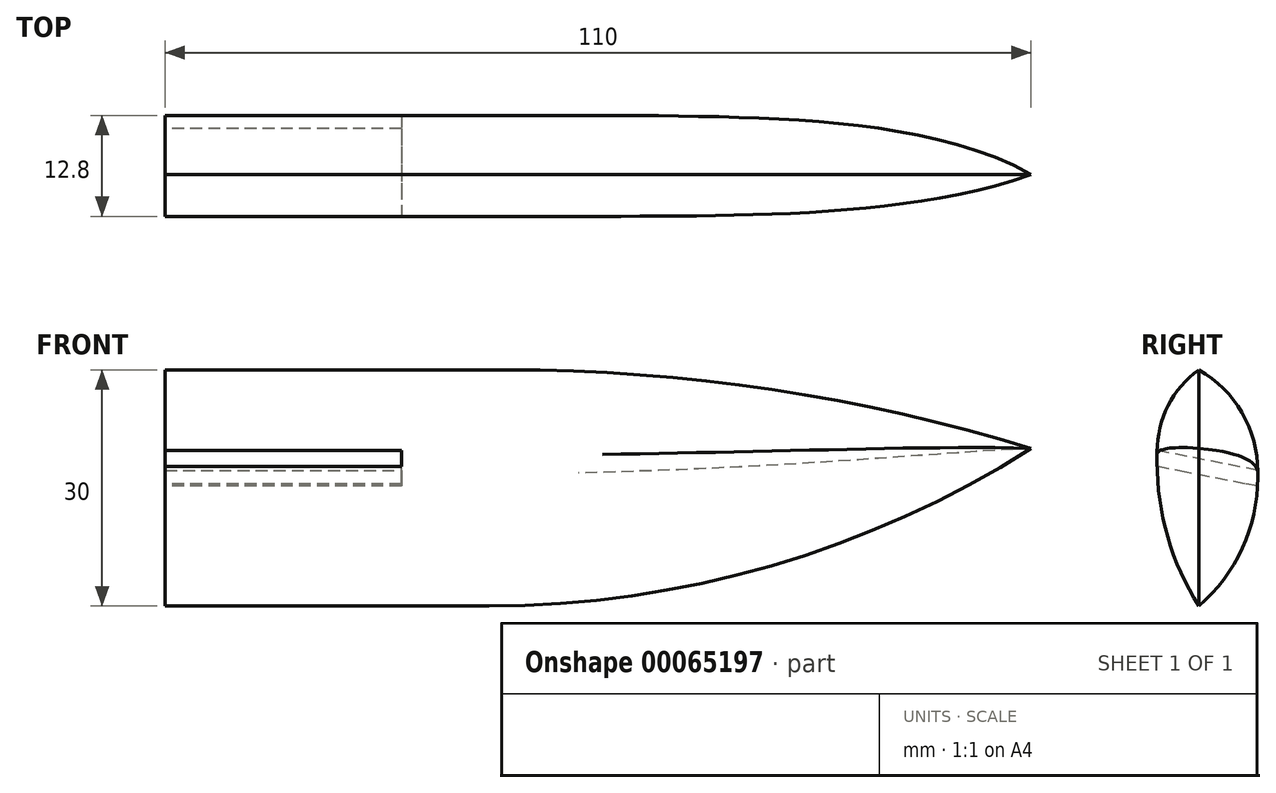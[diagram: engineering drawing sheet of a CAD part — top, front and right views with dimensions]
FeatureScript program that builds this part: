
annotation { "Feature Type Name" : "Feature", "Feature Type Description" : "" }
export const myFeature = defineFeature(function(context is Context, id is Id, definition is map)
    precondition{}
    {
        {
            var Q0;
            Q0=qCreatedBy(makeId("Front.planeOp"),FACE);
            var sketch = newSketch(context, id + "F0", { "sketchPlane" : qUnion([Q0])});
            skLineSegment(sketch, "E0", {"start": v(0, 0) * mm, "end": v(110, 0) * mm});
            skLineSegment(sketch, "E1", {"start": v(110, 0) * mm, "end": v(110, -30) * mm});
            skLineSegment(sketch, "E2", {"start": v(110, -30) * mm, "end": v(0, -30) * mm});
            skLineSegment(sketch, "E3", {"start": v(0, -30) * mm, "end": v(0, 0) * mm});
            skSolve(sketch);
        }
        {
            var Q0;
            Q0 = qSketchRegion(id + "F0", true);
            extrude(context, id + "F1", {"entities" : qUnion([Q0]), "depth" : 5.3 * mm});
        }
        {
            var Q0;
            Q0=makeQuery(id+"F1.opExtrude","SWEPT_EDGE",EDGE,{"disambiguationData":[OSD([sQuery(id+"F0.wireOp",EDGE,"E0"),sQuery(id+"F0.wireOp",EDGE,"E1")])]});
            chamfer(context, id + "F2", {"entities" : qUnion([Q0]), "width" : 20 * mm, "tangentPropagation" : true});
        }
        {
            var Q0;
            Q0=makeQuery(id+"F1.opExtrude","SWEPT_EDGE",EDGE,{"disambiguationData":[OSD([sQuery(id+"F0.wireOp",EDGE,"E1"),sQuery(id+"F0.wireOp",EDGE,"E2")])]});
            chamfer(context, id + "F3", {"entities" : qUnion([Q0]), "width" : 30 * mm, "tangentPropagation" : true});
        }
        {
            var Q0;
            {var subQ0=sQuery(id+"F0.wireOp",EDGE,"E0");Q0=makeQuery(id+"F2.opChamfer","BLEND_EDGE",EDGE,{"blendedFrom":[makeQuery(id+"F1.opExtrude","SWEPT_EDGE",EDGE,{"disambiguationData":[OSD([subQ0,sQuery(id+"F0.wireOp",EDGE,"E1")])]}),makeQuery(id+"F1.opExtrude","SWEPT_FACE",FACE,{"disambiguationData":[OSD([subQ0])]})],"blendedInto":[makeQuery(id+"F1.opExtrude","SWEPT_FACE",FACE,{"disambiguationData":[OSD([subQ0])]})]});}
            fillet(context, id + "F4", {"entities" : qUnion([Q0]), "radius" : 226.64 * mm, "tangentPropagation" : true, "allowEdgeOverflow" : false});
        }
        {
            var Q0;
            {var subQ0=sQuery(id+"F0.wireOp",EDGE,"E2");Q0=makeQuery(id+"F3.opChamfer","BLEND_EDGE",EDGE,{"blendedFrom":[makeQuery(id+"F1.opExtrude","SWEPT_EDGE",EDGE,{"disambiguationData":[OSD([sQuery(id+"F0.wireOp",EDGE,"E1"),subQ0])]}),makeQuery(id+"F1.opExtrude","SWEPT_FACE",FACE,{"disambiguationData":[OSD([subQ0])]})],"blendedInto":[makeQuery(id+"F1.opExtrude","SWEPT_FACE",FACE,{"disambiguationData":[OSD([subQ0])]})]});}
            fillet(context, id + "F5", {"entities" : qUnion([Q0]), "radius" : 128.58 * mm, "tangentPropagation" : true, "allowEdgeOverflow" : false});
        }
        {
            var Q0;
            Q0=makeQuery(id+"F1.opExtrude","CAP_EDGE",EDGE,{"disambiguationData":[OSD([sQuery(id+"F0.wireOp",EDGE,"E0")])],"isStart":false});
            var Q1;
            {var subQ0=sQuery(id+"F0.wireOp",EDGE,"E1");var subQ1=sQuery(id+"F0.wireOp",EDGE,"E0");Q1=makeQuery(id+"F4.opFillet","BLEND_EDGE",EDGE,{"blendedFrom":[makeQuery(id+"F2.opChamfer","BLEND_EDGE",EDGE,{"blendedFrom":[makeQuery(id+"F1.opExtrude","SWEPT_EDGE",EDGE,{"disambiguationData":[OSD([subQ1,subQ0])]}),makeQuery(id+"F1.opExtrude","SWEPT_FACE",FACE,{"disambiguationData":[OSD([subQ1])]})],"blendedInto":[makeQuery(id+"F1.opExtrude","SWEPT_FACE",FACE,{"disambiguationData":[OSD([subQ1])]})]}),makeQuery(id+"F1.opExtrude","CAP_FACE",FACE,{"disambiguationData":[OSD([subQ1,subQ0,sQuery(id+"F0.wireOp",EDGE,"E2"),sQuery(id+"F0.wireOp",EDGE,"E3")])],"isStart":false})],"blendedInto":[makeQuery(id+"F1.opExtrude","CAP_FACE",FACE,{"disambiguationData":[OSD([subQ1,subQ0,sQuery(id+"F0.wireOp",EDGE,"E2"),sQuery(id+"F0.wireOp",EDGE,"E3")])],"isStart":false})]});}
            var Q2;
            {var subQ0=sQuery(id+"F0.wireOp",EDGE,"E1");var subQ1=sQuery(id+"F0.wireOp",EDGE,"E0");var subQ2=sQuery(id+"F0.wireOp",EDGE,"E2");Q2=makeQuery(id+"FQAOI7ziZCkZ1tK_1.opFillet","BLEND_EDGE",EDGE,{"blendedFrom":[makeQuery(id+"F5.opFillet","BLEND_EDGE",EDGE,{"blendedFrom":[makeQuery(id+"F3.opChamfer","BLEND_EDGE",EDGE,{"blendedFrom":[makeQuery(id+"F1.opExtrude","SWEPT_EDGE",EDGE,{"disambiguationData":[OSD([subQ0,subQ2])]}),makeQuery(id+"F1.opExtrude","SWEPT_FACE",FACE,{"disambiguationData":[OSD([subQ2])]})],"blendedInto":[makeQuery(id+"F1.opExtrude","SWEPT_FACE",FACE,{"disambiguationData":[OSD([subQ2])]})]}),makeQuery(id+"F1.opExtrude","CAP_FACE",FACE,{"disambiguationData":[OSD([subQ1,subQ0,subQ2,sQuery(id+"F0.wireOp",EDGE,"E3")])],"isStart":false})],"blendedInto":[makeQuery(id+"F1.opExtrude","CAP_FACE",FACE,{"disambiguationData":[OSD([subQ1,subQ0,subQ2,sQuery(id+"F0.wireOp",EDGE,"E3")])],"isStart":false})]}),makeQuery(id+"F4.opFillet","BLEND_FACE",FACE,{"disambiguationData":[OSD([subQ1,subQ0])]})],"blendedInto":[makeQuery(id+"F4.opFillet","BLEND_FACE",FACE,{"disambiguationData":[OSD([subQ1,subQ0])]})]});}
            fillet(context, id + "F6", {"entities" : qUnion([Q0, Q1, Q2]), "radius" : 12.86 * mm, "tangentPropagation" : true, "allowEdgeOverflow" : false});
        }
        {
            var Q0;
            {var subQ0=makeQuery(id+"F1.opExtrude","SWEPT_FACE",FACE,{"disambiguationData":[OSD([sQuery(id+"F0.wireOp",EDGE,"E3")])]});Q0=makeQuery(id+"FyMCrB8h15b9qGs_1.boolean.opBoolean","MERGE",FACE,{"derivedFrom":[subQ0,makeQuery(id+"FyMCrB8h15b9qGs_1.opPattern","COPY",FACE,{"derivedFrom":subQ0,"instanceName":"1"})]});}
            extrude(context, id + "F7", {"entities" : qUnion([Q0]), "operationType" : NewBodyOperationType.ADD, "depth" : 25 * mm});
        }
        {
            var Q0;
            {var subQ0=sQuery(id+"F0.wireOp",EDGE,"E3");var subQ1=sQuery(id+"F0.wireOp",EDGE,"E2");Q0=makeQuery(id+"F7.boolean.opBoolean","MERGE",EDGE,{"derivedFrom":[makeQuery(id+"F1.opExtrude","CAP_EDGE",EDGE,{"disambiguationData":[OSD([subQ1])],"isStart":false}),makeQuery(id+"F7.opExtrude","SWEPT_EDGE",EDGE,{"disambiguationData":[OSD([subQ1,subQ0]),TDD([makeQuery(id+"F1.opExtrude","CAP_VERTEX",VERTEX,{"disambiguationData":[OSD([subQ1,subQ0])],"isStart":false})])]})]});}
            var Q1;
            {var subQ0=sQuery(id+"F0.wireOp",EDGE,"E2");var subQ1=sQuery(id+"F0.wireOp",EDGE,"E1");Q1=makeQuery(id+"F5.opFillet","BLEND_EDGE",EDGE,{"blendedFrom":[makeQuery(id+"F3.opChamfer","BLEND_EDGE",EDGE,{"blendedFrom":[makeQuery(id+"F1.opExtrude","SWEPT_EDGE",EDGE,{"disambiguationData":[OSD([subQ1,subQ0])]}),makeQuery(id+"F1.opExtrude","SWEPT_FACE",FACE,{"disambiguationData":[OSD([subQ0])]})],"blendedInto":[makeQuery(id+"F1.opExtrude","SWEPT_FACE",FACE,{"disambiguationData":[OSD([subQ0])]})]}),makeQuery(id+"F1.opExtrude","CAP_FACE",FACE,{"disambiguationData":[OSD([sQuery(id+"F0.wireOp",EDGE,"E0"),subQ1,subQ0,sQuery(id+"F0.wireOp",EDGE,"E3")])],"isStart":false})],"blendedInto":[makeQuery(id+"F1.opExtrude","CAP_FACE",FACE,{"disambiguationData":[OSD([sQuery(id+"F0.wireOp",EDGE,"E0"),subQ1,subQ0,sQuery(id+"F0.wireOp",EDGE,"E3")])],"isStart":false})]});}
            var Q2;
            {var subQ0=sQuery(id+"F0.wireOp",EDGE,"E2");var subQ1=sQuery(id+"F0.wireOp",EDGE,"E1");var subQ2=sQuery(id+"F0.wireOp",EDGE,"E0");Q2=makeQuery(id+"F6.opFillet","BLEND_EDGE",EDGE,{"blendedFrom":[makeQuery(id+"F4.opFillet","BLEND_EDGE",EDGE,{"blendedFrom":[makeQuery(id+"F2.opChamfer","BLEND_EDGE",EDGE,{"blendedFrom":[makeQuery(id+"F1.opExtrude","SWEPT_EDGE",EDGE,{"disambiguationData":[OSD([subQ2,subQ1])]}),makeQuery(id+"F1.opExtrude","SWEPT_FACE",FACE,{"disambiguationData":[OSD([subQ2])]})],"blendedInto":[makeQuery(id+"F1.opExtrude","SWEPT_FACE",FACE,{"disambiguationData":[OSD([subQ2])]})]}),makeQuery(id+"F1.opExtrude","CAP_FACE",FACE,{"disambiguationData":[OSD([subQ2,subQ1,subQ0,sQuery(id+"F0.wireOp",EDGE,"E3")])],"isStart":false})],"blendedInto":[makeQuery(id+"F1.opExtrude","CAP_FACE",FACE,{"disambiguationData":[OSD([subQ2,subQ1,subQ0,sQuery(id+"F0.wireOp",EDGE,"E3")])],"isStart":false})]}),makeQuery(id+"F5.opFillet","BLEND_FACE",FACE,{"disambiguationData":[OSD([subQ1,subQ0])]})],"blendedInto":[makeQuery(id+"F5.opFillet","BLEND_FACE",FACE,{"disambiguationData":[OSD([subQ1,subQ0])]})]});}
            fillet(context, id + "F8", {"entities" : qUnion([Q0, Q1, Q2]), "radius" : 34.28 * mm, "tangentPropagation" : true, "allowEdgeOverflow" : false});
        }
        {
            var Q0;
            {var subQ0=makeQuery(id+"F7.opExtrude","CAP_FACE",FACE,{"disambiguationData":[OSD([sQuery(id+"F0.wireOp",EDGE,"E3")])],"isStart":false});Q0=makeQuery(id+"FL7oWuQivoLl6EF_1.boolean.opBoolean","MERGE",FACE,{"derivedFrom":[subQ0,makeQuery(id+"FL7oWuQivoLl6EF_1.opPattern","COPY",FACE,{"derivedFrom":subQ0,"instanceName":"1"})]});}
            extrude(context, id + "F9", {"entities" : qUnion([Q0]), "operationType" : NewBodyOperationType.REMOVE, "oppositeDirection" : true, "depth" : 15 * mm});
        }
        {
            var Q0;
            {var subQ0=sQuery(id+"F0.wireOp",EDGE,"E3");Q0=makeQuery(id+"F7.boolean.opBoolean","MERGE",FACE,{"derivedFrom":[makeQuery(id+"F1.opExtrude","CAP_FACE",FACE,{"disambiguationData":[OSD([sQuery(id+"F0.wireOp",EDGE,"E0"),sQuery(id+"F0.wireOp",EDGE,"E1"),sQuery(id+"F0.wireOp",EDGE,"E2"),subQ0])],"isStart":true}),makeQuery(id+"F7.opExtrude","SWEPT_FACE",FACE,{"disambiguationData":[OSD([subQ0]),TDD([makeQuery(id+"F1.opExtrude","CAP_EDGE",EDGE,{"disambiguationData":[OSD([subQ0])],"isStart":true})])]})]});}
            extrude(context, id + "F10", {"entities" : qUnion([Q0]), "operationType" : NewBodyOperationType.ADD, "depth" : 7.5 * mm});
        }
        {
            var Q0;
            {var subQ0=sQuery(id+"F0.wireOp",EDGE,"E3");Q0=makeQuery(id+"F10.boolean.opBoolean","MERGE",FACE,{"derivedFrom":[makeQuery(id+"F9.boolean.opBoolean","COPY",FACE,{"derivedFrom":makeQuery(id+"F9.opExtrude","CAP_FACE",FACE,{"disambiguationData":[OSD([subQ0])],"isStart":false})}),makeQuery(id+"F10.opExtrude","SWEPT_FACE",FACE,{"disambiguationData":[OSD([subQ0])]})]});}
            var sketch = newSketch(context, id + "F11", { "sketchPlane" : qUnion([Q0])});
            skSolve(sketch);
        }
        {
            var Q0;
            {var subQ0=sQuery(id+"F0.wireOp",EDGE,"E3");var subQ1=sQuery(id+"F0.wireOp",EDGE,"E2");var subQ2=sQuery(id+"F0.wireOp",EDGE,"E1");var subQ3=sQuery(id+"F0.wireOp",EDGE,"E0");Q0=makeQuery(id+"F10.opExtrude","CAP_EDGE",EDGE,{"disambiguationData":[OSD([subQ3,subQ2,subQ1,subQ0]),TDD([makeQuery(id+"F8.opFillet","BLEND_EDGE",EDGE,{"blendedFrom":[makeQuery(id+"F5.opFillet","BLEND_EDGE",EDGE,{"blendedFrom":[makeQuery(id+"F3.opChamfer","BLEND_EDGE",EDGE,{"blendedFrom":[makeQuery(id+"F1.opExtrude","SWEPT_EDGE",EDGE,{"disambiguationData":[OSD([subQ2,subQ1])]}),makeQuery(id+"F1.opExtrude","SWEPT_FACE",FACE,{"disambiguationData":[OSD([subQ1])]})],"blendedInto":[makeQuery(id+"F1.opExtrude","SWEPT_FACE",FACE,{"disambiguationData":[OSD([subQ1])]})]}),makeQuery(id+"F1.opExtrude","CAP_FACE",FACE,{"disambiguationData":[OSD([subQ3,subQ2,subQ1,subQ0])],"isStart":false})],"blendedInto":[makeQuery(id+"F1.opExtrude","CAP_FACE",FACE,{"disambiguationData":[OSD([subQ3,subQ2,subQ1,subQ0])],"isStart":false})]}),makeQuery(id+"F7.boolean.opBoolean","MERGE",FACE,{"derivedFrom":[makeQuery(id+"F1.opExtrude","CAP_FACE",FACE,{"disambiguationData":[OSD([subQ3,subQ2,subQ1,subQ0])],"isStart":true}),makeQuery(id+"F7.opExtrude","SWEPT_FACE",FACE,{"disambiguationData":[OSD([subQ0]),TDD([makeQuery(id+"F1.opExtrude","CAP_EDGE",EDGE,{"disambiguationData":[OSD([subQ0])],"isStart":true})])]})]})],"blendedInto":[makeQuery(id+"F7.boolean.opBoolean","MERGE",FACE,{"derivedFrom":[makeQuery(id+"F1.opExtrude","CAP_FACE",FACE,{"disambiguationData":[OSD([subQ3,subQ2,subQ1,subQ0])],"isStart":true}),makeQuery(id+"F7.opExtrude","SWEPT_FACE",FACE,{"disambiguationData":[OSD([subQ0]),TDD([makeQuery(id+"F1.opExtrude","CAP_EDGE",EDGE,{"disambiguationData":[OSD([subQ0])],"isStart":true})])]})]})]})])],"isStart":false});}
            var Q1;
            {var subQ0=sQuery(id+"F0.wireOp",EDGE,"E3");var subQ1=sQuery(id+"F0.wireOp",EDGE,"E2");var subQ2=sQuery(id+"F0.wireOp",EDGE,"E1");var subQ3=sQuery(id+"F0.wireOp",EDGE,"E0");Q1=makeQuery(id+"F10.opExtrude","CAP_EDGE",EDGE,{"disambiguationData":[OSD([subQ3,subQ2,subQ1,subQ0]),TDD([makeQuery(id+"F8.opFillet","BLEND_EDGE",EDGE,{"blendedFrom":[makeQuery(id+"F7.boolean.opBoolean","MERGE",EDGE,{"derivedFrom":[makeQuery(id+"F1.opExtrude","CAP_EDGE",EDGE,{"disambiguationData":[OSD([subQ1])],"isStart":false}),makeQuery(id+"F7.opExtrude","SWEPT_EDGE",EDGE,{"disambiguationData":[OSD([subQ1,subQ0]),TDD([makeQuery(id+"F1.opExtrude","CAP_VERTEX",VERTEX,{"disambiguationData":[OSD([subQ1,subQ0])],"isStart":false})])]})]}),makeQuery(id+"F7.boolean.opBoolean","MERGE",FACE,{"derivedFrom":[makeQuery(id+"F1.opExtrude","CAP_FACE",FACE,{"disambiguationData":[OSD([subQ3,subQ2,subQ1,subQ0])],"isStart":true}),makeQuery(id+"F7.opExtrude","SWEPT_FACE",FACE,{"disambiguationData":[OSD([subQ0]),TDD([makeQuery(id+"F1.opExtrude","CAP_EDGE",EDGE,{"disambiguationData":[OSD([subQ0])],"isStart":true})])]})]})],"blendedInto":[makeQuery(id+"F7.boolean.opBoolean","MERGE",FACE,{"derivedFrom":[makeQuery(id+"F1.opExtrude","CAP_FACE",FACE,{"disambiguationData":[OSD([subQ3,subQ2,subQ1,subQ0])],"isStart":true}),makeQuery(id+"F7.opExtrude","SWEPT_FACE",FACE,{"disambiguationData":[OSD([subQ0]),TDD([makeQuery(id+"F1.opExtrude","CAP_EDGE",EDGE,{"disambiguationData":[OSD([subQ0])],"isStart":true})])]})]})]})])],"isStart":false});}
            fillet(context, id + "F12", {"entities" : qUnion([Q0, Q1]), "radius" : 21.5 * mm, "tangentPropagation" : true, "allowEdgeOverflow" : false});
        }
        {
            var Q0;
            {var subQ0=sQuery(id+"F0.wireOp",EDGE,"E3");var subQ1=sQuery(id+"F0.wireOp",EDGE,"E2");var subQ2=sQuery(id+"F0.wireOp",EDGE,"E1");var subQ3=sQuery(id+"F0.wireOp",EDGE,"E0");var subQ4=makeQuery(id+"F1.opExtrude","CAP_FACE",FACE,{"disambiguationData":[OSD([subQ3,subQ2,subQ1,subQ0])],"isStart":true});var subQ5=makeQuery(id+"F1.opExtrude","CAP_FACE",FACE,{"disambiguationData":[OSD([subQ3,subQ2,subQ1,subQ0])],"isStart":false});Q0=makeQuery(id+"F12.opFillet","BLEND_EDGE",EDGE,{"blendedFrom":[makeQuery(id+"F10.opExtrude","CAP_EDGE",EDGE,{"disambiguationData":[OSD([subQ3,subQ2,subQ1,subQ0]),TDD([makeQuery(id+"F8.opFillet","BLEND_EDGE",EDGE,{"blendedFrom":[makeQuery(id+"F5.opFillet","BLEND_EDGE",EDGE,{"blendedFrom":[makeQuery(id+"F3.opChamfer","BLEND_EDGE",EDGE,{"blendedFrom":[makeQuery(id+"F1.opExtrude","SWEPT_EDGE",EDGE,{"disambiguationData":[OSD([subQ2,subQ1])]}),makeQuery(id+"F1.opExtrude","SWEPT_FACE",FACE,{"disambiguationData":[OSD([subQ1])]})],"blendedInto":[makeQuery(id+"F1.opExtrude","SWEPT_FACE",FACE,{"disambiguationData":[OSD([subQ1])]})]}),subQ5],"blendedInto":[subQ5]}),makeQuery(id+"F7.boolean.opBoolean","MERGE",FACE,{"derivedFrom":[subQ4,makeQuery(id+"F7.opExtrude","SWEPT_FACE",FACE,{"disambiguationData":[OSD([subQ0]),TDD([makeQuery(id+"F1.opExtrude","CAP_EDGE",EDGE,{"disambiguationData":[OSD([subQ0])],"isStart":true})])]})]})],"blendedInto":[makeQuery(id+"F7.boolean.opBoolean","MERGE",FACE,{"derivedFrom":[subQ4,makeQuery(id+"F7.opExtrude","SWEPT_FACE",FACE,{"disambiguationData":[OSD([subQ0]),TDD([makeQuery(id+"F1.opExtrude","CAP_EDGE",EDGE,{"disambiguationData":[OSD([subQ0])],"isStart":true})])]})]})]})])],"isStart":false}),makeQuery(id+"F10.opExtrude","SWEPT_FACE",FACE,{"disambiguationData":[OSD([subQ3,subQ2,subQ1,subQ0]),TDD([makeQuery(id+"F6.opFillet","BLEND_EDGE",EDGE,{"blendedFrom":[makeQuery(id+"F4.opFillet","BLEND_EDGE",EDGE,{"blendedFrom":[makeQuery(id+"F2.opChamfer","BLEND_EDGE",EDGE,{"blendedFrom":[makeQuery(id+"F1.opExtrude","SWEPT_EDGE",EDGE,{"disambiguationData":[OSD([subQ3,subQ2])]}),makeQuery(id+"F1.opExtrude","SWEPT_FACE",FACE,{"disambiguationData":[OSD([subQ3])]})],"blendedInto":[makeQuery(id+"F1.opExtrude","SWEPT_FACE",FACE,{"disambiguationData":[OSD([subQ3])]})]}),subQ5],"blendedInto":[subQ5]}),subQ4],"blendedInto":[subQ4]})])]})],"blendedInto":[makeQuery(id+"F10.opExtrude","SWEPT_FACE",FACE,{"disambiguationData":[OSD([subQ3,subQ2,subQ1,subQ0]),TDD([makeQuery(id+"F6.opFillet","BLEND_EDGE",EDGE,{"blendedFrom":[makeQuery(id+"F4.opFillet","BLEND_EDGE",EDGE,{"blendedFrom":[makeQuery(id+"F2.opChamfer","BLEND_EDGE",EDGE,{"blendedFrom":[makeQuery(id+"F1.opExtrude","SWEPT_EDGE",EDGE,{"disambiguationData":[OSD([subQ3,subQ2])]}),makeQuery(id+"F1.opExtrude","SWEPT_FACE",FACE,{"disambiguationData":[OSD([subQ3])]})],"blendedInto":[makeQuery(id+"F1.opExtrude","SWEPT_FACE",FACE,{"disambiguationData":[OSD([subQ3])]})]}),subQ5],"blendedInto":[subQ5]}),subQ4],"blendedInto":[subQ4]})])]})]});}
            var Q1;
            {var subQ0=sQuery(id+"F0.wireOp",EDGE,"E3");var subQ1=sQuery(id+"F0.wireOp",EDGE,"E2");var subQ2=sQuery(id+"F0.wireOp",EDGE,"E1");var subQ3=sQuery(id+"F0.wireOp",EDGE,"E0");Q1=makeQuery(id+"F10.opExtrude","CAP_EDGE",EDGE,{"disambiguationData":[OSD([subQ3,subQ2,subQ1,subQ0]),TDD([makeQuery(id+"F6.opFillet","BLEND_EDGE",EDGE,{"blendedFrom":[makeQuery(id+"F4.opFillet","BLEND_EDGE",EDGE,{"blendedFrom":[makeQuery(id+"F2.opChamfer","BLEND_EDGE",EDGE,{"blendedFrom":[makeQuery(id+"F1.opExtrude","SWEPT_EDGE",EDGE,{"disambiguationData":[OSD([subQ3,subQ2])]}),makeQuery(id+"F1.opExtrude","SWEPT_FACE",FACE,{"disambiguationData":[OSD([subQ3])]})],"blendedInto":[makeQuery(id+"F1.opExtrude","SWEPT_FACE",FACE,{"disambiguationData":[OSD([subQ3])]})]}),makeQuery(id+"F1.opExtrude","CAP_FACE",FACE,{"disambiguationData":[OSD([subQ3,subQ2,subQ1,subQ0])],"isStart":false})],"blendedInto":[makeQuery(id+"F1.opExtrude","CAP_FACE",FACE,{"disambiguationData":[OSD([subQ3,subQ2,subQ1,subQ0])],"isStart":false})]}),makeQuery(id+"F1.opExtrude","CAP_FACE",FACE,{"disambiguationData":[OSD([subQ3,subQ2,subQ1,subQ0])],"isStart":true})],"blendedInto":[makeQuery(id+"F1.opExtrude","CAP_FACE",FACE,{"disambiguationData":[OSD([subQ3,subQ2,subQ1,subQ0])],"isStart":true})]})])],"isStart":false});}
            var Q2;
            {var subQ0=sQuery(id+"F0.wireOp",EDGE,"E3");var subQ1=sQuery(id+"F0.wireOp",EDGE,"E2");var subQ2=sQuery(id+"F0.wireOp",EDGE,"E1");var subQ3=sQuery(id+"F0.wireOp",EDGE,"E0");var subQ4=makeQuery(id+"F1.opExtrude","CAP_FACE",FACE,{"disambiguationData":[OSD([subQ3,subQ2,subQ1,subQ0])],"isStart":true});var subQ5=makeQuery(id+"F1.opExtrude","CAP_EDGE",EDGE,{"disambiguationData":[OSD([subQ3])],"isStart":false});Q2=makeQuery(id+"F10.opExtrude","CAP_EDGE",EDGE,{"disambiguationData":[OSD([subQ3,subQ2,subQ1,subQ0]),TDD([makeQuery(id+"F7.boolean.opBoolean","MERGE",EDGE,{"derivedFrom":[makeQuery(id+"F6.opFillet","BLEND_EDGE",EDGE,{"blendedFrom":[subQ5,subQ4],"blendedInto":[subQ4]}),makeQuery(id+"F7.opExtrude","SWEPT_EDGE",EDGE,{"disambiguationData":[OSD([subQ3,subQ2,subQ1,subQ0]),TDD([makeQuery(id+"F6.opFillet","BLEND_VERTEX",VERTEX,{"blendedFrom":[subQ5,makeQuery(id+"F1.opExtrude","SWEPT_FACE",FACE,{"disambiguationData":[OSD([subQ0])]}),subQ4],"blendedInto":[makeQuery(id+"F1.opExtrude","SWEPT_FACE",FACE,{"disambiguationData":[OSD([subQ0])]}),subQ4]})])]})]})])],"isStart":false});}
            fillet(context, id + "F13", {"entities" : qUnion([Q0, Q1, Q2]), "radius" : 14.87 * mm, "tangentPropagation" : true, "allowEdgeOverflow" : false});
        }
        {
            var Q0;
            {var subQ0=sQuery(id+"F0.wireOp",EDGE,"E3");Q0=makeQuery(id+"F11.imprint","IMPRINT",FACE,{"disambiguationData":[TD([[makeQuery(id+"F11.imprint","IMPRINT",EDGE,{"derivedFrom":makeQuery(id+"F10.opExtrude","CAP_EDGE",EDGE,{"disambiguationData":[OSD([subQ0])],"isStart":false})}),-1.0]])]});}
            var sketch = newSketch(context, id + "F14", { "sketchPlane" : qUnion([Q0])});
            skLineSegment(sketch, "E4", {"start": v(-9.45, -15.15) * mm, "end": v(-9.45, -13.15) * mm});
            skLineSegment(sketch, "E5", {"start": v(7.25, -9.88) * mm, "end": v(7.25, -11.88) * mm});
            skLineSegment(sketch, "E6", {"start": v(-9.45, -13.15) * mm, "end": v(7.25, -9.88) * mm});
            skLineSegment(sketch, "E7", {"start": v(-5.86, -14.49) * mm, "end": v(1.54, -13.04) * mm});
            skLineSegment(sketch, "E8", {"start": v(1.54, -13.04) * mm, "end": v(7.25, -11.88) * mm});
            skLineSegment(sketch, "E9", {"start": v(-9.45, -15.15) * mm, "end": v(-5.86, -14.49) * mm});
            skSolve(sketch);
        }
        {
            var Q0;
            Q0 = qSketchRegion(id + "F14", true);
            extrude(context, id + "F15", {"entities" : qUnion([Q0]), "operationType" : NewBodyOperationType.REMOVE, "oppositeDirection" : true, "depth" : 30 * mm});
        }
    });
